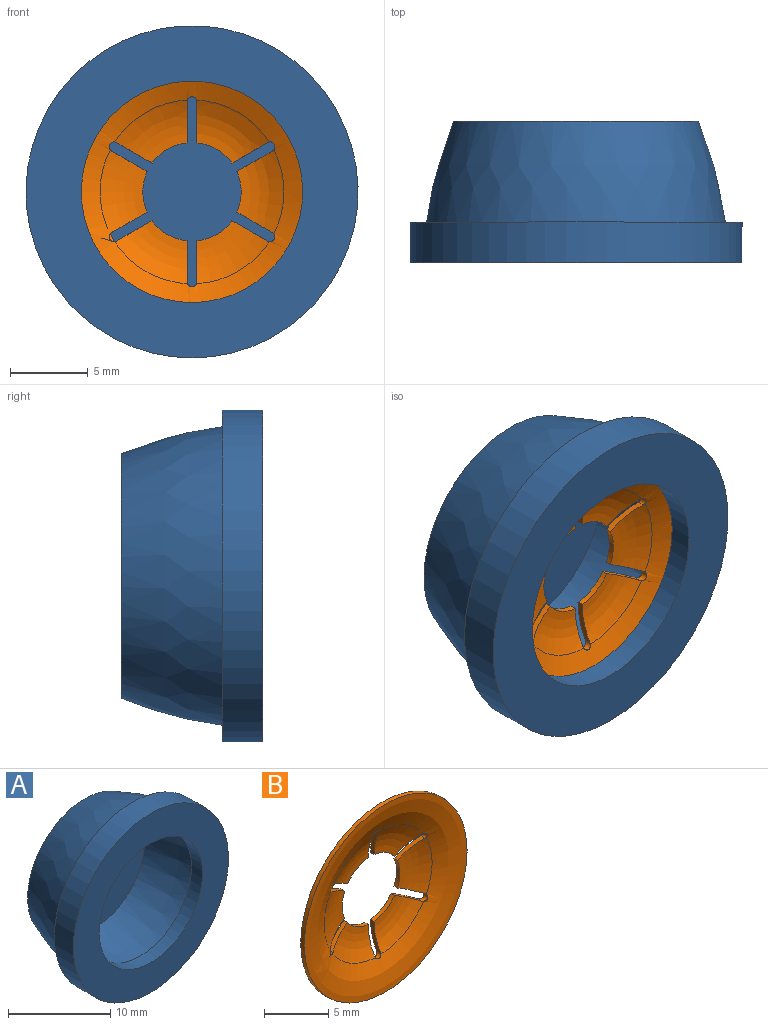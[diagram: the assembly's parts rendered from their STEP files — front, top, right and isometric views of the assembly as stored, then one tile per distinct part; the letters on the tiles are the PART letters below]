
ASSEMBLY  parts=2 mates=1
PART A: 11 faces, bbox 21.4x9.1x21.4 mm
  f0: plane 13.38x13.38mm, normal (0,-1,0), area 140.6mm2, adj f1
  f1: revolved ~16.07x16.07mm, area 275.9mm2, adj f0,f2
  f2: plane 17.86x17.86mm, normal (0,-1,0), area 47.6mm2, adj f1,f3
  f3: cylinder r=8.93mm len=17.86mm, axis (0,-1,0), area 21.4mm2, adj f2,f4
  f4: plane 17.86x17.86mm, normal (0,1,0), area 90.2mm2, adj f3,f5
  f5: cylinder r=7.14mm len=14.29mm, axis (0,-1,0), area 68.4mm2, adj f4,f6
  f6: plane 21.43x21.43mm, normal (0,-1,0), area 200.4mm2, adj f5,f7
  f7: cylinder r=10.72mm len=21.43mm, axis (0,-1,0), area 175.6mm2, adj f6,f8
  f8: plane 21.43x21.43mm, normal (0,1,0), area 68.5mm2, adj f7,f9
  f9: revolved ~19.29x19.29mm, area 379.1mm2, adj f8,f10
  f10: plane 15.79x15.79mm, normal (0,1,0), area 195.9mm2, adj f9
PART B: 39 faces, bbox 17.9x2.1x17.9 mm
  f0: revolved ~17.83x17.8mm, area 146.3mm2, adj f13,f14,f15,f16,f17,f18,f20,f21
  f1: torus R=3.17mm, axis (0,-1,0), area 13.3mm2, adj f8,f19,f30,f32,f33,f34
  f2: torus R=3.17mm, axis (0,-1,0), area 13.3mm2, adj f7,f19,f21,f23,f33,f35
  f3: torus R=3.17mm, axis (0,-1,0), area 13.3mm2, adj f10,f19,f30,f31,f36,f38
  f4: torus R=3.17mm, axis (0,-1,0), area 13.3mm2, adj f11,f19,f27,f29,f37,f38
  f5: torus R=3.17mm, axis (0,-1,0), area 13.3mm2, adj f12,f19,f24,f25,f27,f28
  f6: torus R=3.17mm, axis (0,-1,0), area 13.3mm2, adj f9,f19,f21,f22,f24,f26
  f7: cylinder r=3.17mm len=2.26mm, axis (0,-1,0), area 1mm2, adj f2,f13,f23,f35
  f8: cylinder r=3.17mm len=2.61mm, axis (0,-1,0), area 1mm2, adj f1,f14,f32,f34
  f9: cylinder r=3.17mm len=2.26mm, axis (0,-1,0), area 1mm2, adj f6,f18,f22,f26
  f10: cylinder r=3.17mm len=2.26mm, axis (0,-1,0), area 1mm2, adj f3,f15,f31,f36
  f11: cylinder r=3.17mm len=2.26mm, axis (0,-1,0), area 1mm2, adj f4,f16,f29,f37
  f12: cylinder r=3.17mm len=2.61mm, axis (0,-1,0), area 1mm2, adj f5,f17,f25,f28
  f13: torus R=3.17mm, axis (0,-1,0), area 12mm2, adj f0,f7,f21,f23,f33,f35
  f14: torus R=3.17mm, axis (0,-1,0), area 12mm2, adj f0,f8,f30,f32,f33,f34
  f15: torus R=3.17mm, axis (0,-1,0), area 12mm2, adj f0,f10,f30,f31,f36,f38
  f16: torus R=3.17mm, axis (0,-1,0), area 12mm2, adj f0,f11,f27,f29,f37,f38
  f17: torus R=3.17mm, axis (0,-1,0), area 12mm2, adj f0,f12,f24,f25,f27,f28
  f18: torus R=3.17mm, axis (0,-1,0), area 12mm2, adj f0,f9,f21,f22,f24,f26
  f19: revolved ~17.82x17.82mm, area 138.6mm2, adj f1,f2,f3,f4,f5,f6,f20,f24
  f20: cylinder r=8.93mm len=17.86mm, axis (0,-1,0), area 21.4mm2, adj f0,f19
  f21: cylinder r=0.32mm len=0.64mm, axis (0,-1,0), area 0.5mm2, adj f0,f2,f6,f13,f18,f22,f23
  f22: plane 2.73x1.16mm, normal (1,0,0), area 1.1mm2, adj f6,f9,f18,f21
  f23: plane 2.73x1.16mm, normal (-1,0,0), area 1.1mm2, adj f2,f7,f13,f21
  f24: cylinder r=0.32mm len=0.61mm, axis (0,-1,0), area 0.5mm2, adj f0,f5,f6,f17,f18,f19,f25,f26
  f25: plane 2.37x1.4mm, normal (0.5,0,-0.87), area 1.1mm2, adj f5,f12,f17,f24
  f26: plane 2.37x1.4mm, normal (-0.5,0,0.87), area 1.1mm2, adj f6,f9,f18,f24
  f27: cylinder r=0.32mm len=0.61mm, axis (0,-1,0), area 0.4mm2, adj f0,f4,f5,f16,f17,f19,f28,f29
  f28: plane 2.37x1.4mm, normal (0.5,0,0.87), area 1.1mm2, adj f5,f12,f17,f27
  f29: plane 2.37x1.4mm, normal (-0.5,0,-0.87), area 1.1mm2, adj f4,f11,f16,f27
  f30: cylinder r=0.32mm len=0.61mm, axis (0,-1,0), area 0.4mm2, adj f0,f1,f3,f14,f15,f19,f31,f32
  f31: plane 2.37x1.4mm, normal (0.5,0,-0.87), area 1.1mm2, adj f3,f10,f15,f30
  f32: plane 2.37x1.4mm, normal (-0.5,0,0.87), area 1.1mm2, adj f1,f8,f14,f30
  f33: cylinder r=0.32mm len=0.61mm, axis (0,-1,0), area 0.4mm2, adj f0,f1,f2,f13,f14,f19,f34,f35
  f34: plane 2.37x1.4mm, normal (-0.5,0,-0.87), area 1.1mm2, adj f1,f8,f14,f33
  f35: plane 2.37x1.4mm, normal (0.5,0,0.87), area 1.1mm2, adj f2,f7,f13,f33
  f36: plane 2.73x1.16mm, normal (-1,0,0), area 1.1mm2, adj f3,f10,f15,f38
  f37: plane 2.73x1.16mm, normal (1,0,0), area 1.1mm2, adj f4,f11,f16,f38
  f38: cylinder r=0.32mm len=0.64mm, axis (0,-1,0), area 0.5mm2, adj f0,f3,f4,f15,f16,f36,f37
PLACE A t=(0,-1.39,0)mm
PLACE B t=(0,-1.6,0)mm
MATE fastened B.f7 <-> A.f3  axis (0,-1,0) through (0,-1.39,0)mm
